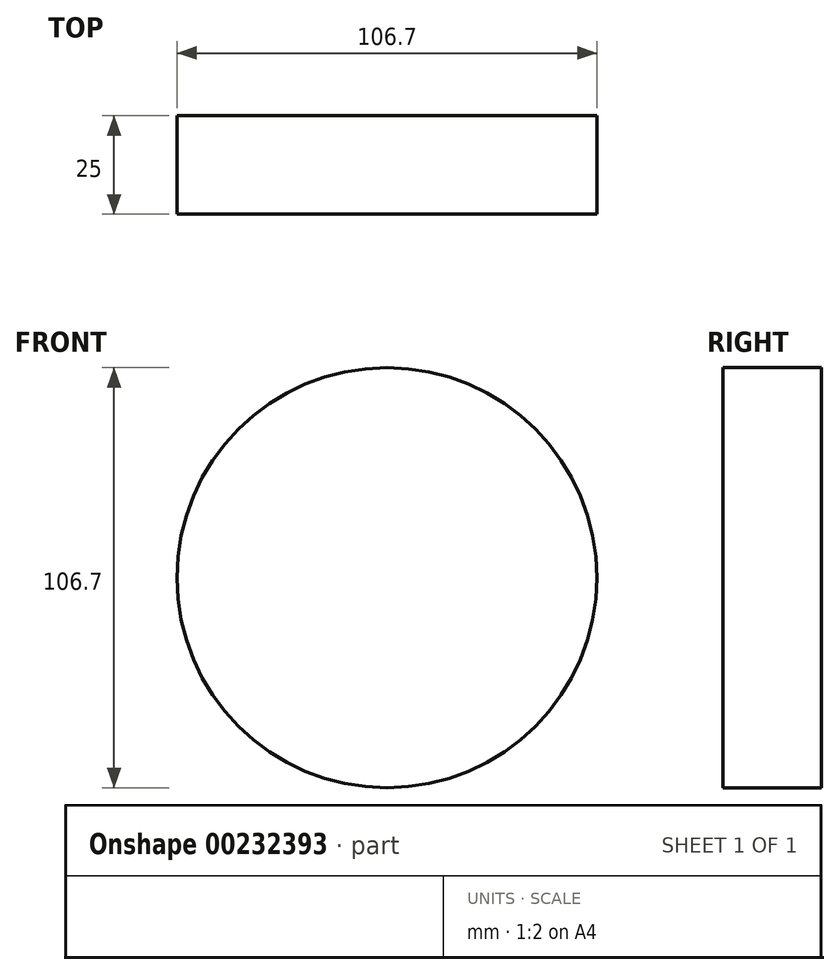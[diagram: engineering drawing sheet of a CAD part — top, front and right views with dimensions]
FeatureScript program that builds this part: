
annotation { "Feature Type Name" : "Feature", "Feature Type Description" : "" }
export const myFeature = defineFeature(function(context is Context, id is Id, definition is map)
    precondition{}
    {
        {
            var Q0;
            Q0=qCreatedBy(makeId("Front.planeOp"),FACE);
            var sketch = newSketch(context, id + "F0", { "sketchPlane" : qUnion([Q0])});
            skCircle(sketch, "E0", {"center": v(0, 0) * mm, "radius": 53.35 * mm});
            skCircle(sketch, "E1", {"center": v(77.15, -19.6) * mm, "radius": 35.55 * mm, "construction": true});
            skSolve(sketch);
        }
        {
            var Q0;
            Q0 = qSketchRegion(id + "F0", true);
            extrude(context, id + "F1", {"entities" : qUnion([Q0]), "depth" : 25 * mm});
        }
    });
